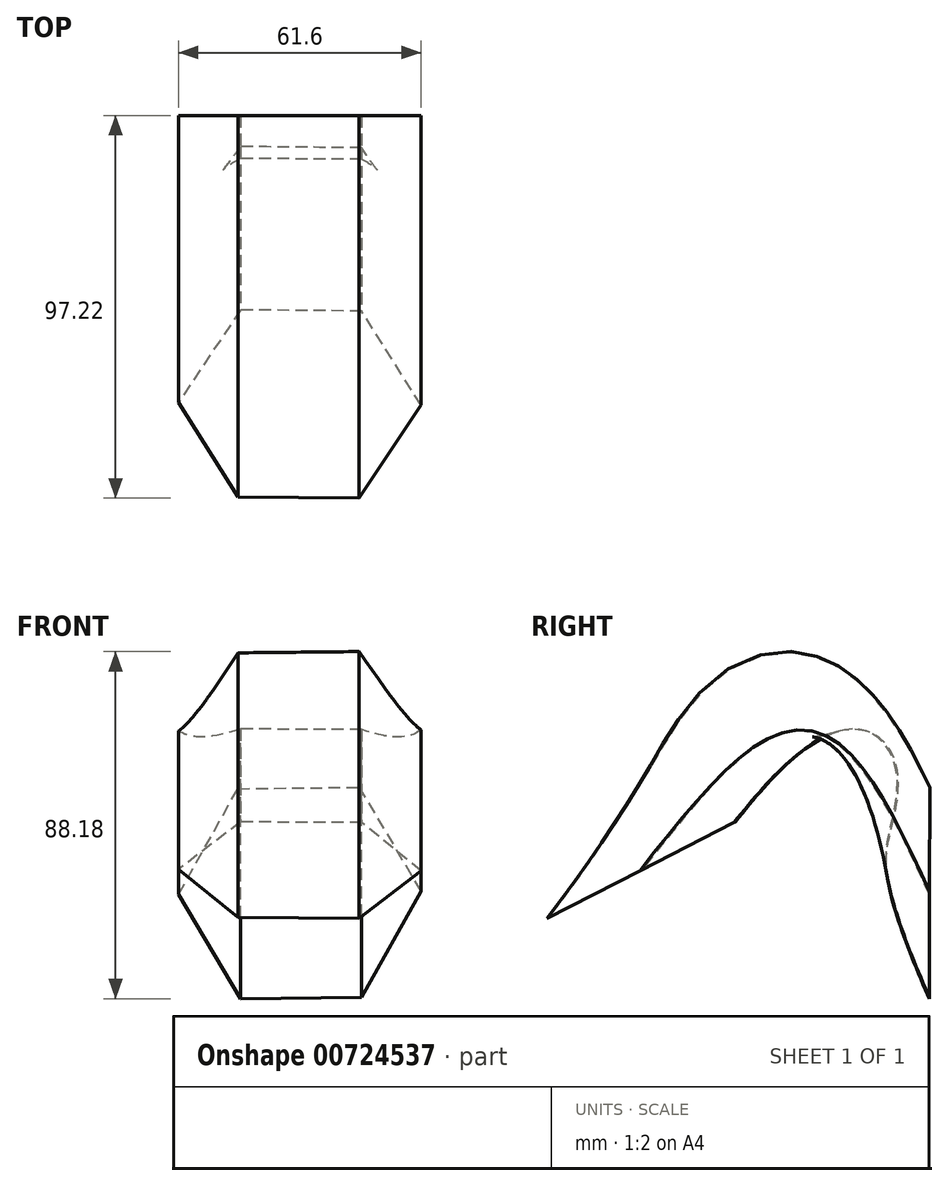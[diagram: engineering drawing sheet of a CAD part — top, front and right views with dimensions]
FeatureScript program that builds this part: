
annotation { "Feature Type Name" : "Feature", "Feature Type Description" : "" }
export const myFeature = defineFeature(function(context is Context, id is Id, definition is map)
    precondition{}
    {
        {
            var Q0;
            Q0=qCreatedBy(makeId("Front.planeOp"),FACE);
            var sketch = newSketch(context, id + "F0", { "sketchPlane" : qUnion([Q0])});
            skCircle(sketch, "E0.cCircle", {"center": v(-45.59, 33.6) * mm, "radius": 26.68 * mm, "construction": true});
            skLineSegment(sketch, "E0.0", {"start": v(-60.68, 6.75) * mm, "end": v(-76.4, 33.25) * mm});
            skLineSegment(sketch, "E0.1", {"start": v(-76.4, 33.25) * mm, "end": v(-61.3, 60.1) * mm});
            skLineSegment(sketch, "E0.2", {"start": v(-61.3, 60.1) * mm, "end": v(-30.5, 60.46) * mm});
            skLineSegment(sketch, "E0.3", {"start": v(-30.5, 60.46) * mm, "end": v(-14.79, 33.97) * mm});
            skLineSegment(sketch, "E0.4", {"start": v(-14.79, 33.97) * mm, "end": v(-29.88, 7.11) * mm});
            skLineSegment(sketch, "E0.5", {"start": v(-29.88, 7.11) * mm, "end": v(-60.68, 6.75) * mm});
            skPoint(sketch, "E0.0.midPoint", {"position": v(-68.54, 20) * mm});
            skSolve(sketch);
        }
        {
            var Q0;
            Q0=qCreatedBy(makeId("Right.planeOp"),FACE);
            var sketch = newSketch(context, id + "F1", { "sketchPlane" : qUnion([Q0])});
            skFitSpline(sketch, "E1", {"points": [v(-1.73, 30.16) * mm, v(-30.36, 69.35) * mm, v(-69.96, 34.83) * mm], "startDerivative": vector(-53.7, 116.15) * mm, "endDerivative": vector(-82.57, -105.35) * mm});
            skSolve(sketch);
        }
        {
            var Q0;
            Q0=makeQuery(id+"F0.imprint","IMPRINT",FACE,{"disambiguationData":[TD([[makeQuery(id+"F0.imprint","IMPRINT",EDGE,{"derivedFrom":sQuery(id+"F0.wireOp",EDGE,"E0.0")}),-1.0]])]});
            var Q1;
            Q1=sQuery(id+"F1.wireOp",EDGE,"E1");
            sweep(context, id + "F2", {"profiles" : qUnion([Q0]), "path" : qUnion([Q1])});
        }
    });
